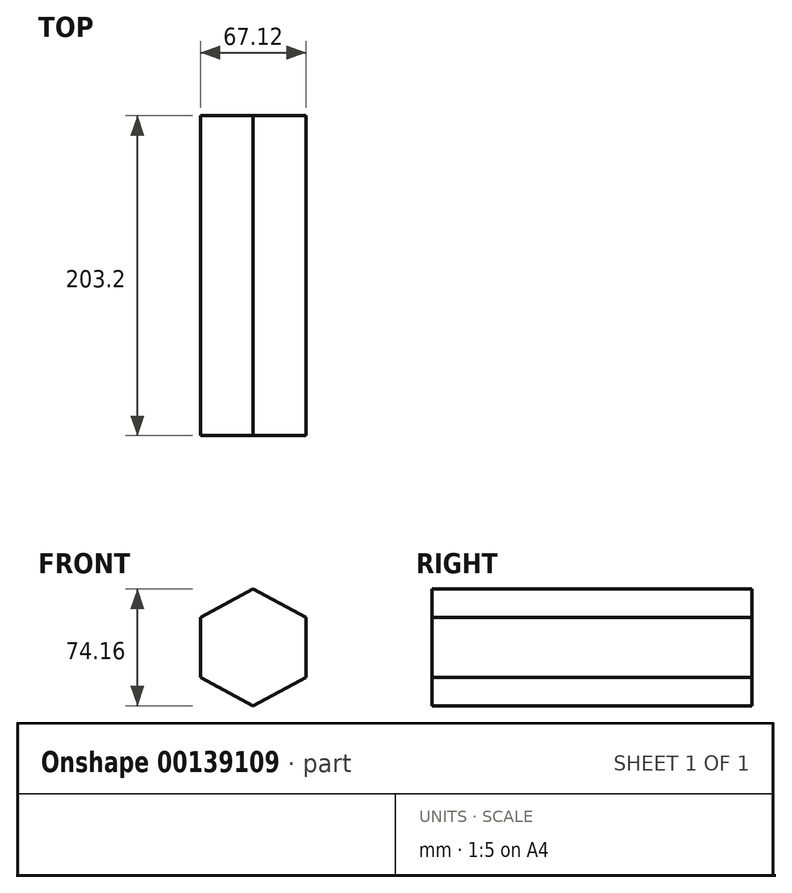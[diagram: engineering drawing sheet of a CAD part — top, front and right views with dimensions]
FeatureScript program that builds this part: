
annotation { "Feature Type Name" : "Feature", "Feature Type Description" : "" }
export const myFeature = defineFeature(function(context is Context, id is Id, definition is map)
    precondition{}
    {
        {
            var Q0;
            Q0=qCreatedBy(makeId("Front.planeOp"),FACE);
            var sketch = newSketch(context, id + "F0", { "sketchPlane" : qUnion([Q0])});
            skLineSegment(sketch, "E0", {"start": v(-51.9, 38.1) * mm, "end": v(-51.9, 0) * mm});
            skLineSegment(sketch, "E1", {"start": v(-51.9, 38.1) * mm, "end": v(-18.35, 56.13) * mm});
            skLineSegment(sketch, "E2", {"start": v(-18.35, 56.13) * mm, "end": v(15.21, 38.1) * mm});
            skLineSegment(sketch, "E3", {"start": v(15.21, 38.1) * mm, "end": v(15.21, 0) * mm});
            skLineSegment(sketch, "E4", {"start": v(15.21, 0) * mm, "end": v(-18.35, -18.03) * mm});
            skLineSegment(sketch, "E5", {"start": v(-18.35, -18.03) * mm, "end": v(-51.9, 0) * mm});
            skSolve(sketch);
        }
        {
            var Q0;
            Q0 = qSketchRegion(id + "F0", true);
            extrude(context, id + "F1", {"entities" : qUnion([Q0]), "depth" : 203.2 * mm});
        }
    });
